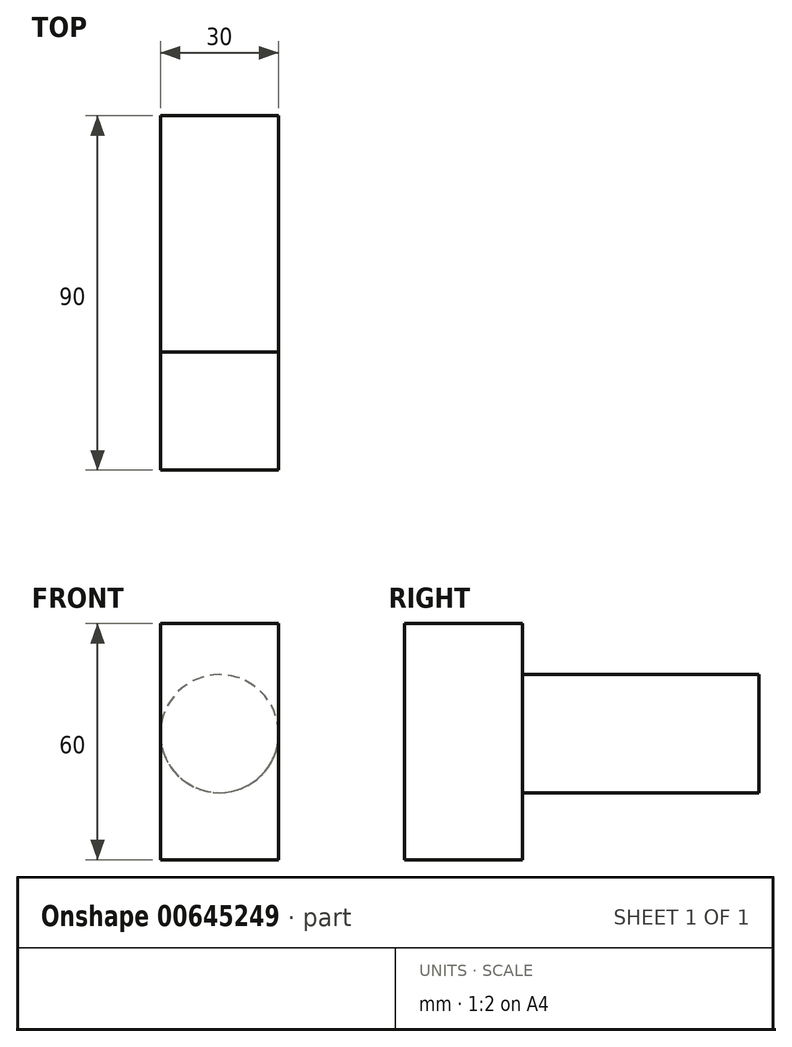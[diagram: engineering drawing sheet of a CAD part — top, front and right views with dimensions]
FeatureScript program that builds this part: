
annotation { "Feature Type Name" : "Feature", "Feature Type Description" : "" }
export const myFeature = defineFeature(function(context is Context, id is Id, definition is map)
    precondition{}
    {
        {
            var Q0;
            Q0=qCreatedBy(makeId("Front.planeOp"),FACE);
            var sketch = newSketch(context, id + "F0", { "sketchPlane" : qUnion([Q0])});
            skLineSegment(sketch, "E0.bottom", {"start": v(-22.3, 27.99) * mm, "end": v(7.7, 27.99) * mm});
            skLineSegment(sketch, "E0.top", {"start": v(-22.3, -32.01) * mm, "end": v(7.7, -32.01) * mm});
            skLineSegment(sketch, "E0.left", {"start": v(-22.3, 27.99) * mm, "end": v(-22.3, -32.01) * mm});
            skLineSegment(sketch, "E0.right", {"start": v(7.7, 27.99) * mm, "end": v(7.7, -32.01) * mm});
            skLineSegment(sketch, "E1", {"start": v(7.7, 0) * mm, "end": v(-22.3, 0) * mm, "construction": true});
            skLineSegment(sketch, "E2", {"start": v(-7.3, 27.99) * mm, "end": v(-7.3, -32.01) * mm, "construction": true});
            skCircle(sketch, "E3", {"center": v(-7.3, 0) * mm, "radius": 15 * mm});
            skSolve(sketch);
        }
        {
            var Q0;
            Q0 = qSketchRegion(id + "F0", true);
            extrude(context, id + "F1", {"entities" : qUnion([Q0]), "depth" : 30 * mm, "offsetDistance" : 25.4 * mm});
        }
        {
            var Q0;
            {var subQ0=sQuery(id+"F0.wireOp",EDGE,"E3");var subQ1=makeQuery(id+"F0.imprint","INTERSECT",VERTEX,{"derivedFrom":[sQuery(id+"F0.wireOp",EDGE,"E0.left"),subQ0]});Q0=makeQuery(id+"F0.imprint","IMPRINT",FACE,{"disambiguationData":[TD([[makeQuery(id+"F0.imprint","IMPRINT",EDGE,{"disambiguationData":[TD([[subQ1,1.0]])],"derivedFrom":subQ0}),1.0]])]});}
            extrude(context, id + "F2", {"entities" : qUnion([Q0]), "operationType" : NewBodyOperationType.ADD, "oppositeDirection" : true, "depth" : 60 * mm, "offsetDistance" : 25.4 * mm});
        }
    });
